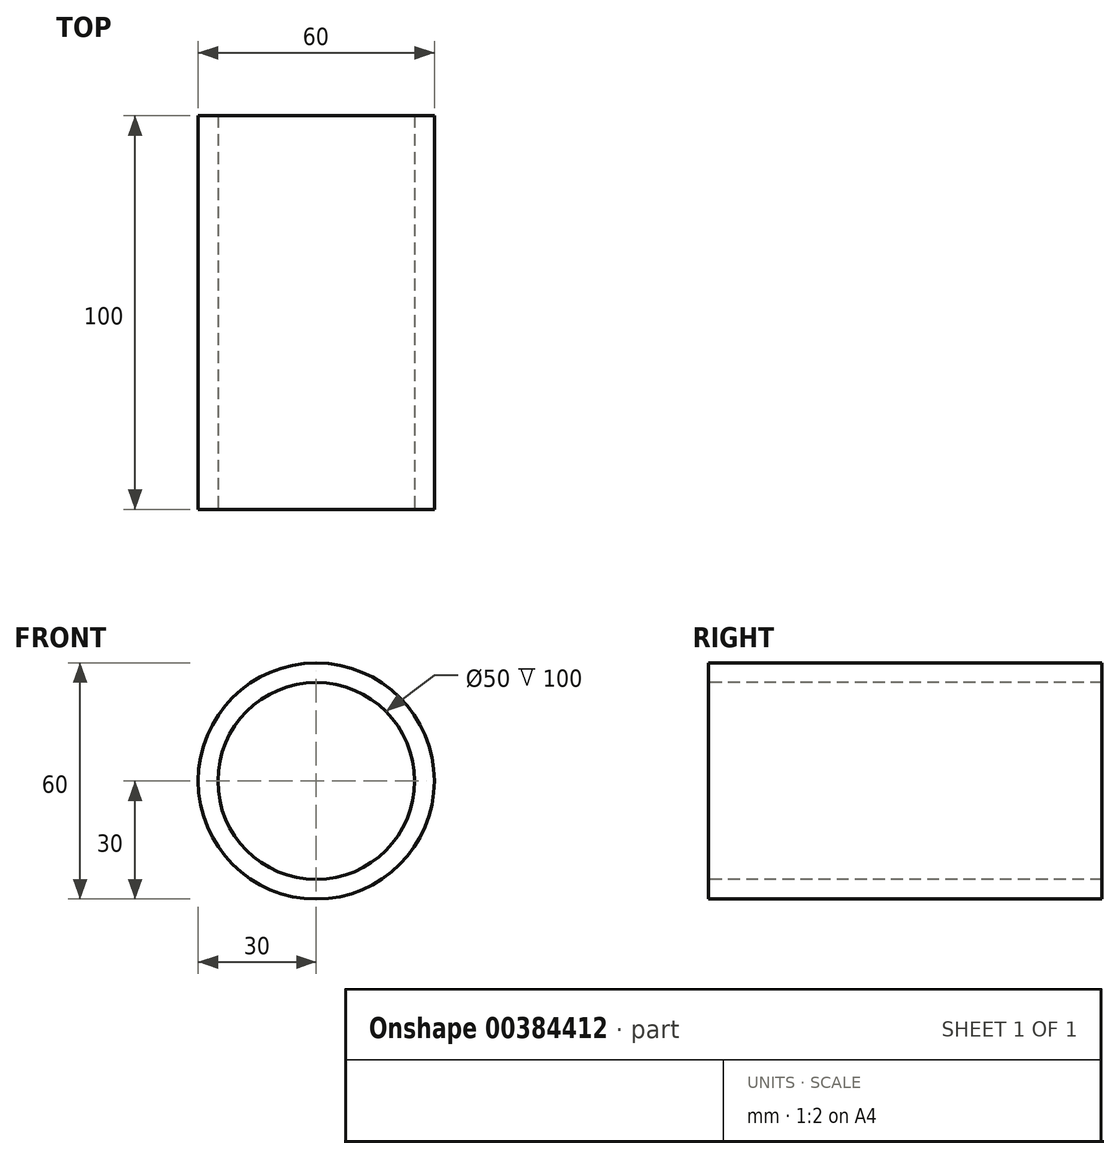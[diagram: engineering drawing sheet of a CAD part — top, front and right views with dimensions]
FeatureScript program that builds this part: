
annotation { "Feature Type Name" : "Feature", "Feature Type Description" : "" }
export const myFeature = defineFeature(function(context is Context, id is Id, definition is map)
    precondition{}
    {
        {
            var Q0;
            Q0=qCreatedBy(makeId("Front.planeOp"),FACE);
            var sketch = newSketch(context, id + "F0", { "sketchPlane" : qUnion([Q0])});
            skCircle(sketch, "E0", {"center": v(0, 0) * mm, "radius": 30 * mm});
            skCircle(sketch, "E1", {"center": v(0, 0) * mm, "radius": 25 * mm});
            skSolve(sketch);
        }
        {
            var Q0;
            Q0 = qSketchRegion(id + "F0", true);
            extrude(context, id + "F1", {"entities" : qUnion([Q0]), "oppositeDirection" : true, "depth" : 100 * mm});
        }
    });
